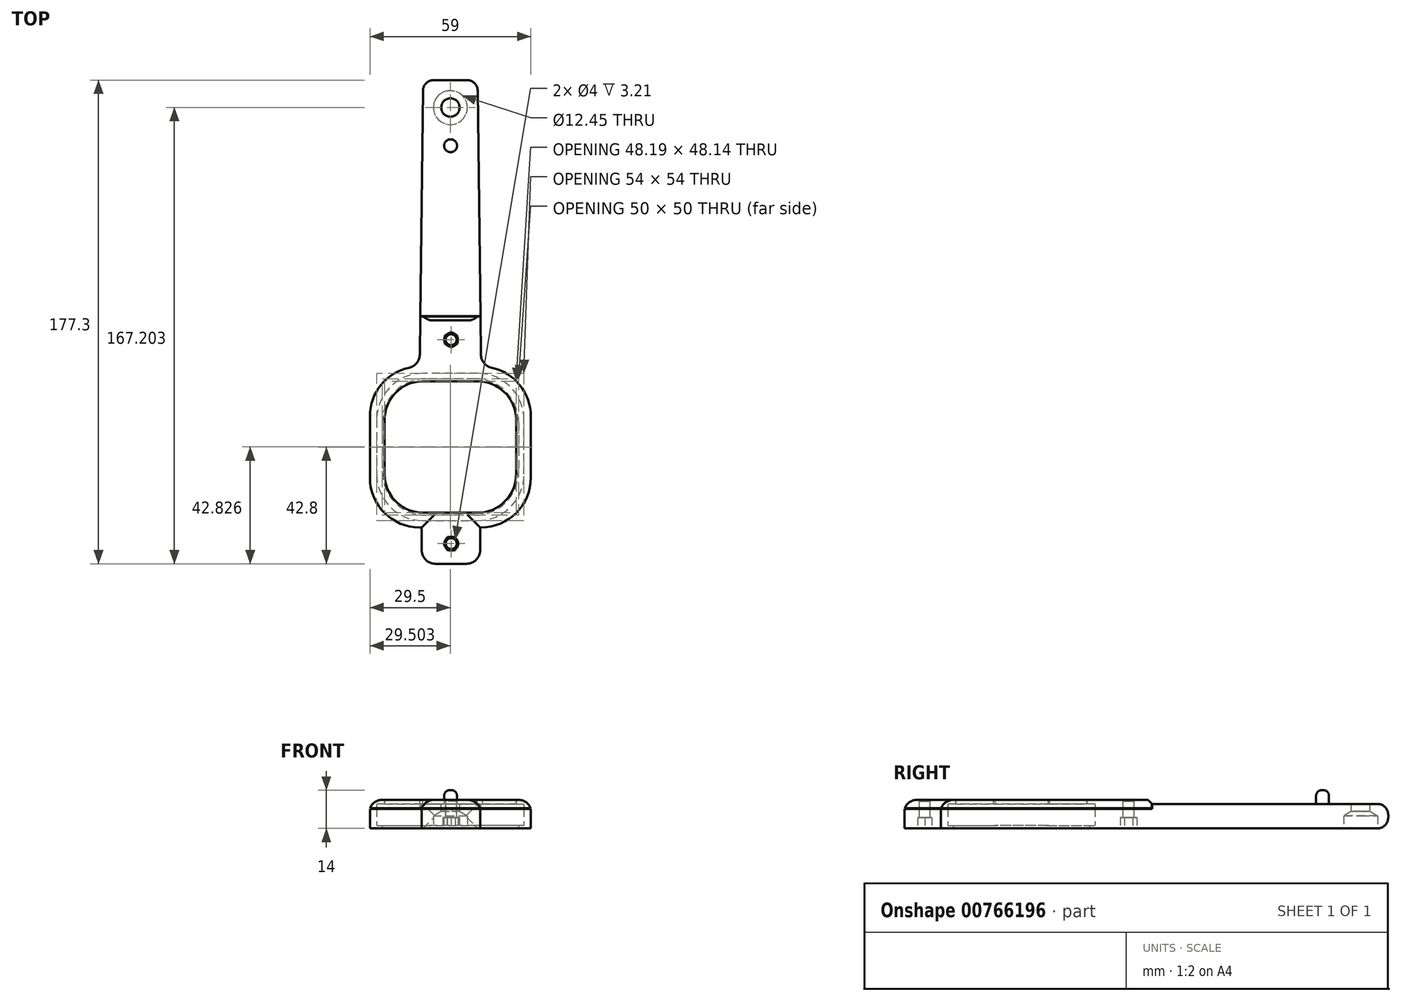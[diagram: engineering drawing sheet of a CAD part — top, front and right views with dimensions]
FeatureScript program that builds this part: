
annotation { "Feature Type Name" : "Feature", "Feature Type Description" : "" }
export const myFeature = defineFeature(function(context is Context, id is Id, definition is map)
    precondition{}
    {
        {
            var Q0;
            Q0=qCreatedBy(makeId("Top.planeOp"),FACE);
            var sketch = newSketch(context, id + "F0", { "sketchPlane" : qUnion([Q0])});
            skLineSegment(sketch, "E0.bottom", {"start": v(17, 0) * mm, "end": v(37, 0) * mm});
            skLineSegment(sketch, "E0.top", {"start": v(17, -54) * mm, "end": v(37, -54) * mm});
            skLineSegment(sketch, "E0.left", {"start": v(0, -17) * mm, "end": v(0, -37) * mm});
            skLineSegment(sketch, "E0.right", {"start": v(54, -17) * mm, "end": v(54, -37) * mm});
            skPoint(sketch, "E1.visualSharp", {"position": v(0, 0) * mm});
            skArc(sketch, "E1.filletArc", {"start": v(17, 0) * mm, "mid": v(4.98, -4.98) * mm, "end": v(0, -17) * mm});
            skPoint(sketch, "E2.visualSharp", {"position": v(54, 0) * mm});
            skArc(sketch, "E2.filletArc", {"start": v(54, -17) * mm, "mid": v(49.02, -4.98) * mm, "end": v(37, 0) * mm});
            skPoint(sketch, "E3.visualSharp", {"position": v(54, -54) * mm});
            skArc(sketch, "E3.filletArc", {"start": v(37, -54) * mm, "mid": v(49.02, -49.02) * mm, "end": v(54, -37) * mm});
            skPoint(sketch, "E4.visualSharp", {"position": v(0, -54) * mm});
            skArc(sketch, "E4.filletArc", {"start": v(0, -37) * mm, "mid": v(4.98, -49.02) * mm, "end": v(17, -54) * mm});
            skLineSegment(sketch, "E5.bottom", {"start": v(15.75, 2.5) * mm, "end": v(38.25, 2.5) * mm});
            skLineSegment(sketch, "E5.top", {"start": v(15.75, -56.5) * mm, "end": v(38.25, -56.5) * mm});
            skLineSegment(sketch, "E5.left", {"start": v(-2.5, -15.75) * mm, "end": v(-2.5, -38.25) * mm});
            skLineSegment(sketch, "E5.right", {"start": v(56.5, -15.75) * mm, "end": v(56.5, -38.25) * mm});
            skPoint(sketch, "E6.visualSharp", {"position": v(-2.5, 2.5) * mm});
            skArc(sketch, "E6.filletArc", {"start": v(15.75, 2.5) * mm, "mid": v(2.85, -2.85) * mm, "end": v(-2.5, -15.75) * mm});
            skPoint(sketch, "E7.visualSharp", {"position": v(56.5, 2.5) * mm});
            skArc(sketch, "E7.filletArc", {"start": v(56.5, -15.75) * mm, "mid": v(51.15, -2.85) * mm, "end": v(38.25, 2.5) * mm});
            skPoint(sketch, "E8.visualSharp", {"position": v(56.5, -56.5) * mm});
            skArc(sketch, "E8.filletArc", {"start": v(38.25, -56.5) * mm, "mid": v(51.15, -51.15) * mm, "end": v(56.5, -38.25) * mm});
            skPoint(sketch, "E9.visualSharp", {"position": v(-2.5, -56.5) * mm});
            skArc(sketch, "E9.filletArc", {"start": v(-2.5, -38.25) * mm, "mid": v(2.85, -51.15) * mm, "end": v(15.75, -56.5) * mm});
            skLineSegment(sketch, "E10", {"start": v(38.25, 2.5) * mm, "end": v(37, 107.5) * mm});
            skLineSegment(sketch, "E11", {"start": v(37, 107.5) * mm, "end": v(17, 107.5) * mm});
            skLineSegment(sketch, "E12", {"start": v(17, 107.5) * mm, "end": v(15.75, 2.5) * mm});
            skPoint(sketch, "E13.startSnap0", {"position": v(27, 107.5) * mm});
            skPoint(sketch, "E13.end.orphan", {"position": v(27, 107.5) * mm});
            skPoint(sketch, "E13.start.orphan", {"position": v(27, 2.5) * mm});
            skSolve(sketch);
        }
        {
            var Q0;
            Q0=makeQuery(id+"F0.imprint","IMPRINT",FACE,{"disambiguationData":[TD([[makeQuery(id+"F0.imprint","IMPRINT",EDGE,{"derivedFrom":sQuery(id+"F0.wireOp",EDGE,"E0.bottom")}),1.0]])]});
            extrude(context, id + "F1", {"entities" : qUnion([Q0]), "depth" : 9 * mm, "offsetDistance" : 25 * mm});
        }
        {
            var Q0;
            Q0=makeQuery(id+"F1.opExtrude","CAP_FACE",FACE,{"disambiguationData":[OSD([sQuery(id+"F0.wireOp",EDGE,"E0.bottom"),sQuery(id+"F0.wireOp",EDGE,"E0.top"),sQuery(id+"F0.wireOp",EDGE,"E0.left"),sQuery(id+"F0.wireOp",EDGE,"E0.right"),sQuery(id+"F0.wireOp",EDGE,"E1.filletArc"),sQuery(id+"F0.wireOp",EDGE,"E2.filletArc"),sQuery(id+"F0.wireOp",EDGE,"E3.filletArc"),sQuery(id+"F0.wireOp",EDGE,"E4.filletArc"),sQuery(id+"F0.wireOp",EDGE,"E5.bottom"),sQuery(id+"F0.wireOp",EDGE,"E5.top"),sQuery(id+"F0.wireOp",EDGE,"E5.left"),sQuery(id+"F0.wireOp",EDGE,"E5.right"),sQuery(id+"F0.wireOp",EDGE,"E6.filletArc"),sQuery(id+"F0.wireOp",EDGE,"E7.filletArc"),sQuery(id+"F0.wireOp",EDGE,"E8.filletArc"),sQuery(id+"F0.wireOp",EDGE,"E9.filletArc")])],"isStart":true});
            var sketch = newSketch(context, id + "F2", { "sketchPlane" : qUnion([Q0])});
            skLineSegment(sketch, "E14.bottom", {"start": v(37.7, 0) * mm, "end": v(16.48, 0) * mm});
            skLineSegment(sketch, "E14.top", {"start": v(37.7, 56) * mm, "end": v(16.48, 56) * mm});
            skLineSegment(sketch, "E14.left", {"start": v(55.96, 18.25) * mm, "end": v(55.96, 37.75) * mm});
            skLineSegment(sketch, "E14.right", {"start": v(-1.77, 18.25) * mm, "end": v(-1.77, 37.75) * mm});
            skPoint(sketch, "E15.visualSharp", {"position": v(-1.77, 0) * mm});
            skArc(sketch, "E15.filletArc", {"start": v(-1.77, 18.25) * mm, "mid": v(3.58, 5.35) * mm, "end": v(16.48, 0) * mm});
            skPoint(sketch, "E16.visualSharp", {"position": v(-1.77, 56) * mm});
            skArc(sketch, "E16.filletArc", {"start": v(16.48, 56) * mm, "mid": v(3.58, 50.65) * mm, "end": v(-1.77, 37.75) * mm});
            skPoint(sketch, "E17.visualSharp", {"position": v(55.96, 56) * mm});
            skArc(sketch, "E17.filletArc", {"start": v(55.96, 37.75) * mm, "mid": v(50.61, 50.65) * mm, "end": v(37.7, 56) * mm});
            skPoint(sketch, "E18.visualSharp", {"position": v(55.96, 0) * mm});
            skArc(sketch, "E18.filletArc", {"start": v(37.7, 0) * mm, "mid": v(50.61, 5.35) * mm, "end": v(55.96, 18.25) * mm});
            skLineSegment(sketch, "E19.bottom", {"start": v(36, 2) * mm, "end": v(18, 2) * mm});
            skLineSegment(sketch, "E19.top", {"start": v(36, 52) * mm, "end": v(18, 52) * mm});
            skLineSegment(sketch, "E19.left", {"start": v(52, 18) * mm, "end": v(52, 36) * mm});
            skLineSegment(sketch, "E19.right", {"start": v(2, 18) * mm, "end": v(2, 36) * mm});
            skPoint(sketch, "E20.visualSharp", {"position": v(52, 2) * mm});
            skArc(sketch, "E20.filletArc", {"start": v(36, 2) * mm, "mid": v(47.31, 6.69) * mm, "end": v(52, 18) * mm});
            skPoint(sketch, "E21.visualSharp", {"position": v(2, 2) * mm});
            skArc(sketch, "E21.filletArc", {"start": v(2, 18) * mm, "mid": v(6.69, 6.69) * mm, "end": v(18, 2) * mm});
            skPoint(sketch, "E22.visualSharp", {"position": v(2, 52) * mm});
            skArc(sketch, "E22.filletArc", {"start": v(18, 52) * mm, "mid": v(6.69, 47.31) * mm, "end": v(2, 36) * mm});
            skPoint(sketch, "E23.visualSharp", {"position": v(52, 52) * mm});
            skArc(sketch, "E23.filletArc", {"start": v(52, 36) * mm, "mid": v(47.31, 47.31) * mm, "end": v(36, 52) * mm});
            skSolve(sketch);
        }
        {
            var Q0;
            Q0=makeQuery(id+"F2.imprint","IMPRINT",FACE,{"disambiguationData":[TD([[makeQuery(id+"F2.imprint","IMPRINT",EDGE,{"derivedFrom":sQuery(id+"F2.wireOp",EDGE,"E19.bottom")}),1.0]])]});
            extrude(context, id + "F3", {"entities" : qUnion([Q0]), "operationType" : NewBodyOperationType.ADD, "oppositeDirection" : true, "depth" : 1 * mm, "offsetDistance" : 25 * mm});
        }
        {
            var Q0;
            Q0=makeQuery(id+"F1.opExtrude","CAP_FACE",FACE,{"disambiguationData":[OSD([sQuery(id+"F0.wireOp",EDGE,"E0.bottom"),sQuery(id+"F0.wireOp",EDGE,"E0.top"),sQuery(id+"F0.wireOp",EDGE,"E0.left"),sQuery(id+"F0.wireOp",EDGE,"E0.right"),sQuery(id+"F0.wireOp",EDGE,"E1.filletArc"),sQuery(id+"F0.wireOp",EDGE,"E2.filletArc"),sQuery(id+"F0.wireOp",EDGE,"E3.filletArc"),sQuery(id+"F0.wireOp",EDGE,"E4.filletArc"),sQuery(id+"F0.wireOp",EDGE,"E5.bottom"),sQuery(id+"F0.wireOp",EDGE,"E5.top"),sQuery(id+"F0.wireOp",EDGE,"E5.left"),sQuery(id+"F0.wireOp",EDGE,"E5.right"),sQuery(id+"F0.wireOp",EDGE,"E6.filletArc"),sQuery(id+"F0.wireOp",EDGE,"E7.filletArc"),sQuery(id+"F0.wireOp",EDGE,"E8.filletArc"),sQuery(id+"F0.wireOp",EDGE,"E9.filletArc")])],"isStart":false});
            var sketch = newSketch(context, id + "F4", { "sketchPlane" : qUnion([Q0])});
            skLineSegment(sketch, "E24.bottom", {"start": v(15.75, -56.5) * mm, "end": v(38.68, -56.5) * mm});
            skLineSegment(sketch, "E24.top", {"start": v(15.75, -51) * mm, "end": v(38.68, -51) * mm});
            skLineSegment(sketch, "E24.left", {"start": v(15.75, -56.5) * mm, "end": v(15.75, -51) * mm});
            skLineSegment(sketch, "E24.right", {"start": v(38.68, -56.5) * mm, "end": v(38.68, -51) * mm});
            skPoint(sketch, "E25", {"position": v(27.03, 97.4) * mm});
            skLineSegment(sketch, "E26.0", {"start": v(37, 107.5) * mm, "end": v(17, 107.5) * mm});
            skSolve(sketch);
        }
        {
            var Q0;
            {var subQ5=makeQuery(id+"F1.opExtrude","CAP_EDGE",EDGE,{"disambiguationData":[OSD([sQuery(id+"F0.wireOp",EDGE,"E0.top")])],"isStart":false});Q0=makeQuery(id+"F4.imprint","IMPRINT",FACE,{"disambiguationData":[TD([[makeQuery(id+"F4.imprint","IMPRINT",EDGE,{"derivedFrom":subQ5}),-1.0]])]});}
            var Q1;
            {var subQ2=sQuery(id+"F4.wireOp",EDGE,"E24.top");Q1=makeQuery(id+"F4.imprint","IMPRINT",FACE,{"disambiguationData":[TD([[makeQuery(id+"F4.imprint","IMPRINT",EDGE,{"derivedFrom":subQ2}),-1.0]])]});}
            extrude(context, id + "F5", {"entities" : qUnion([Q0, Q1]), "operationType" : NewBodyOperationType.ADD, "depth" : 1.5 * mm, "offsetDistance" : 25 * mm});
        }
        {
            var Q0;
            Q0=makeQuery(id+"F0.imprint","IMPRINT",FACE,{"disambiguationData":[TD([[makeQuery(id+"F0.imprint","IMPRINT",EDGE,{"derivedFrom":sQuery(id+"F0.wireOp",EDGE,"E5.bottom")}),1.0]])]});
            extrude(context, id + "F6", {"entities" : qUnion([Q0]), "operationType" : NewBodyOperationType.ADD, "depth" : 9 * mm, "offsetDistance" : 25 * mm});
        }
        {
            var Q0;
            {var subQ0=sQuery(id+"F0.wireOp",EDGE,"E10");var subQ1=sQuery(id+"F0.wireOp",EDGE,"E7.filletArc");var subQ2=sQuery(id+"F0.wireOp",EDGE,"E5.bottom");Q0=makeQuery(id+"F6.boolean.opBoolean","MERGE",EDGE,{"derivedFrom":[makeQuery(id+"Fi0xQTKt3oh8g8N_1.boolean.opBoolean","MERGE",EDGE,{"derivedFrom":[makeQuery(id+"F1.opExtrude","SWEPT_EDGE",EDGE,{"disambiguationData":[OSD([subQ2,subQ1,subQ0])]}),makeQuery(id+"Fi0xQTKt3oh8g8N_1.opExtrude","SWEPT_EDGE",EDGE,{"disambiguationData":[OSD([subQ1,sQuery(id+"Fwkhj9xOdCnqwH3_1.wireOp",EDGE,"TBOp4eyl-GCsp-HRSN-tsRw-HrjPXPLde6vr.bottom")])]})]}),makeQuery(id+"F6.opExtrude","SWEPT_EDGE",EDGE,{"disambiguationData":[OSD([subQ2,subQ1,subQ0])]})]});}
            var Q1;
            {var subQ0=sQuery(id+"F0.wireOp",EDGE,"E12");var subQ1=sQuery(id+"F0.wireOp",EDGE,"E6.filletArc");var subQ2=sQuery(id+"F0.wireOp",EDGE,"E5.bottom");Q1=makeQuery(id+"F6.boolean.opBoolean","MERGE",EDGE,{"derivedFrom":[makeQuery(id+"F1.opExtrude","SWEPT_EDGE",EDGE,{"disambiguationData":[OSD([subQ2,subQ1,subQ0])]}),makeQuery(id+"F6.opExtrude","SWEPT_EDGE",EDGE,{"disambiguationData":[OSD([subQ2,subQ1,subQ0])]})]});}
            fillet(context, id + "F7", {"entities" : qUnion([Q0, Q1]), "radius" : 5 * mm, "tangentPropagation" : true, "allowEdgeOverflow" : false});
        }
        {
            var Q0;
            Q0=sQuery(id+"F4.wireOp",VERTEX,"E25");
            var Q1;
            Q1=makeQuery(id+"F1.opExtrude","SWEPT_BODY",BODY,{"disambiguationData":[OSD([sQuery(id+"F0.wireOp",EDGE,"E0.bottom"),sQuery(id+"F0.wireOp",EDGE,"E0.top"),sQuery(id+"F0.wireOp",EDGE,"E0.left"),sQuery(id+"F0.wireOp",EDGE,"E0.right"),sQuery(id+"F0.wireOp",EDGE,"E1.filletArc"),sQuery(id+"F0.wireOp",EDGE,"E2.filletArc"),sQuery(id+"F0.wireOp",EDGE,"E3.filletArc"),sQuery(id+"F0.wireOp",EDGE,"E4.filletArc"),sQuery(id+"F0.wireOp",EDGE,"E5.bottom"),sQuery(id+"F0.wireOp",EDGE,"E5.top"),sQuery(id+"F0.wireOp",EDGE,"E5.left"),sQuery(id+"F0.wireOp",EDGE,"E5.right"),sQuery(id+"F0.wireOp",EDGE,"E6.filletArc"),sQuery(id+"F0.wireOp",EDGE,"E7.filletArc"),sQuery(id+"F0.wireOp",EDGE,"E8.filletArc"),sQuery(id+"F0.wireOp",EDGE,"E9.filletArc")])]});
            hole(context, id + "F8", {"style" : HoleStyle.SIMPLE, "endStyle" : HoleEndStyle.BLIND, "standardTappedOrClearance" : lookupTablePath({ "fit" : "Free", "standard" : "ANSI", "size" : "1/4", "type" : "Clearance" }), "standardBlindInLast" : lookupTablePath({ "fit" : "Free", "standard" : "ANSI", "size" : "1/4", "type" : "Clearance" }), "holeDiameter" : 6.76 * mm, "majorDiameter" : 5 * mm, "holeDepth" : 50 * mm, "isTappedThrough" : true, "tappedDepth" : 12 * mm, "tapClearance" : 3, "locations" : qUnion([Q0]), "scope" : qUnion([Q1])});
        }
        {
            var Q0;
            Q0=makeQuery(id+"F0.imprint","IMPRINT",FACE,{"disambiguationData":[TD([[makeQuery(id+"F0.imprint","IMPRINT",EDGE,{"derivedFrom":sQuery(id+"F0.wireOp",EDGE,"E5.bottom")}),1.0]])]});
            var sketch = newSketch(context, id + "F9", { "sketchPlane" : qUnion([Q0])});
            skPoint(sketch, "E27", {"position": v(27, 97.4) * mm});
            skLineSegment(sketch, "E28", {"start": v(16.85, 83.42) * mm, "end": v(37.33, 83.42) * mm});
            skPoint(sketch, "E29", {"position": v(27.09, 83.42) * mm});
            skCircle(sketch, "E30", {"center": v(27.09, 83.42) * mm, "radius": 2.38 * mm});
            skPoint(sketch, "E31.0", {"position": v(27.03, 97.4) * mm});
            skSolve(sketch);
        }
        {
            var Q0;
            Q0=sQuery(id+"F9.wireOp",VERTEX,"E27");
            var Q1;
            Q1=makeQuery(id+"F1.opExtrude","SWEPT_BODY",BODY,{"disambiguationData":[OSD([sQuery(id+"F0.wireOp",EDGE,"E0.bottom"),sQuery(id+"F0.wireOp",EDGE,"E0.top"),sQuery(id+"F0.wireOp",EDGE,"E0.left"),sQuery(id+"F0.wireOp",EDGE,"E0.right"),sQuery(id+"F0.wireOp",EDGE,"E1.filletArc"),sQuery(id+"F0.wireOp",EDGE,"E2.filletArc"),sQuery(id+"F0.wireOp",EDGE,"E3.filletArc"),sQuery(id+"F0.wireOp",EDGE,"E4.filletArc"),sQuery(id+"F0.wireOp",EDGE,"E5.bottom"),sQuery(id+"F0.wireOp",EDGE,"E5.top"),sQuery(id+"F0.wireOp",EDGE,"E5.left"),sQuery(id+"F0.wireOp",EDGE,"E5.right"),sQuery(id+"F0.wireOp",EDGE,"E6.filletArc"),sQuery(id+"F0.wireOp",EDGE,"E7.filletArc"),sQuery(id+"F0.wireOp",EDGE,"E8.filletArc"),sQuery(id+"F0.wireOp",EDGE,"E9.filletArc")])]});
            hole(context, id + "F10", {"style" : HoleStyle.SIMPLE, "endStyle" : HoleEndStyle.BLIND, "oppositeDirection" : true, "holeDiameter" : 12.45 * mm, "majorDiameter" : 5 * mm, "holeDepth" : 4.57 * mm, "isTappedThrough" : true, "tappedDepth" : 12 * mm, "tapClearance" : 3, "locations" : qUnion([Q0]), "scope" : qUnion([Q1])});
        }
        {
            var Q0;
            {var subQ0=sQuery(id+"F0.wireOp",EDGE,"E5.bottom");var subQ1=sQuery(id+"F0.wireOp",EDGE,"E6.filletArc");var subQ2=sQuery(id+"F0.wireOp",EDGE,"E5.left");var subQ3=sQuery(id+"F0.wireOp",EDGE,"E5.top");var subQ4=sQuery(id+"F0.wireOp",EDGE,"E0.bottom");var subQ5=sQuery(id+"F0.wireOp",EDGE,"E0.left");var subQ6=sQuery(id+"F0.wireOp",EDGE,"E4.filletArc");var subQ8=sQuery(id+"F0.wireOp",EDGE,"E9.filletArc");var subQ11=sQuery(id+"F0.wireOp",EDGE,"E8.filletArc");var subQ12=sQuery(id+"F0.wireOp",EDGE,"E1.filletArc");var subQ14=sQuery(id+"F0.wireOp",EDGE,"E7.filletArc");Q0=makeQuery(id+"F6.boolean.opBoolean","MERGE",FACE,{"derivedFrom":[makeQuery(id+"F5.boolean.opBoolean","SPLIT",FACE,{"disambiguationData":[TD([makeQuery(id+"F1.opExtrude","SWEPT_FACE",FACE,{"disambiguationData":[OSD([subQ4])]})])],"derivedFrom":makeQuery(id+"F1.opExtrude","CAP_FACE",FACE,{"disambiguationData":[OSD([subQ4,sQuery(id+"F0.wireOp",EDGE,"E0.top"),subQ5,sQuery(id+"F0.wireOp",EDGE,"E0.right"),subQ12,sQuery(id+"F0.wireOp",EDGE,"E2.filletArc"),sQuery(id+"F0.wireOp",EDGE,"E3.filletArc"),subQ6,subQ0,subQ3,subQ2,sQuery(id+"F0.wireOp",EDGE,"E5.right"),subQ1,subQ14,subQ11,subQ8])],"isStart":false})}),makeQuery(id+"F6.opExtrude","CAP_FACE",FACE,{"disambiguationData":[OSD([subQ0,sQuery(id+"F0.wireOp",EDGE,"E10"),sQuery(id+"F0.wireOp",EDGE,"E11"),sQuery(id+"F0.wireOp",EDGE,"E12")])],"isStart":false})]});}
            var sketch = newSketch(context, id + "F11", { "sketchPlane" : qUnion([Q0])});
            skCircle(sketch, "E32", {"center": v(27.09, 83.42) * mm, "radius": 2.36 * mm});
            skCircle(sketch, "E33.0", {"center": v(27.09, 83.42) * mm, "radius": 2.38 * mm});
            skSolve(sketch);
        }
        {
            var Q0;
            {var subQ0=sQuery(id+"F11.wireOp",EDGE,"E33.0");var subQ1=sQuery(id+"F11.wireOp",EDGE,"E32");var subQ2=makeQuery(id+"F11.imprint","INTERSECT",VERTEX,{"disambiguationData":[OD(0.0)],"derivedFrom":[subQ1,subQ0]});Q0=makeQuery(id+"F11.imprint","IMPRINT",FACE,{"disambiguationData":[TD([[makeQuery(id+"F11.imprint","IMPRINT",EDGE,{"disambiguationData":[TD([[subQ2,1.0]])],"derivedFrom":subQ1}),1.0]])]});}
            extrude(context, id + "F12", {"entities" : qUnion([Q0]), "operationType" : NewBodyOperationType.ADD, "depth" : 5 * mm, "offsetDistance" : 25 * mm});
        }
        {
            var Q0;
            Q0=makeQuery(id+"F12.opExtrude","CAP_EDGE",EDGE,{"disambiguationData":[OSD([sQuery(id+"F11.wireOp",EDGE,"E32")])],"isStart":false});
            fillet(context, id + "F13", {"entities" : qUnion([Q0]), "radius" : 2 * mm, "tangentPropagation" : true, "allowEdgeOverflow" : false});
        }
        {
            var Q0;
            Q0=makeQuery(id+"F6.opExtrude","CAP_EDGE",EDGE,{"disambiguationData":[OSD([sQuery(id+"F0.wireOp",EDGE,"E11")])],"isStart":false});
            var Q1;
            Q1=makeQuery(id+"F6.opExtrude","SWEPT_EDGE",EDGE,{"disambiguationData":[OSD([sQuery(id+"F0.wireOp",EDGE,"E11"),sQuery(id+"F0.wireOp",EDGE,"E12")])]});
            var Q2;
            Q2=makeQuery(id+"F6.opExtrude","SWEPT_EDGE",EDGE,{"disambiguationData":[OSD([sQuery(id+"F0.wireOp",EDGE,"E10"),sQuery(id+"F0.wireOp",EDGE,"E11")])]});
            var Q3;
            Q3=makeQuery(id+"F6.opExtrude","CAP_EDGE",EDGE,{"disambiguationData":[OSD([sQuery(id+"F0.wireOp",EDGE,"E11")])],"isStart":true});
            fillet(context, id + "F14", {"entities" : qUnion([Q0, Q1, Q2, Q3]), "radius" : 4 * mm, "allowEdgeOverflow" : false});
        }
        {
            var Q0;
            Q0=makeQuery(id+"F5.opExtrude","CAP_FACE",FACE,{"disambiguationData":[OSD([sQuery(id+"F0.wireOp",EDGE,"E8.filletArc"),sQuery(id+"F4.wireOp",EDGE,"E24.bottom"),sQuery(id+"F4.wireOp",EDGE,"E24.top"),sQuery(id+"F4.wireOp",EDGE,"E24.left"),sQuery(id+"F4.wireOp",EDGE,"E24.right")])],"isStart":false});
            var sketch = newSketch(context, id + "F15", { "sketchPlane" : qUnion([Q0])});
            skLineSegment(sketch, "E34", {"start": v(16.5, -56.5) * mm, "end": v(16.5, -69.8) * mm});
            skLineSegment(sketch, "E35", {"start": v(16.5, -69.8) * mm, "end": v(37.93, -69.8) * mm});
            skLineSegment(sketch, "E36", {"start": v(37.93, -69.8) * mm, "end": v(37.93, -56.5) * mm});
            skPoint(sketch, "E37", {"position": v(27.33, -62.41) * mm});
            skPoint(sketch, "E38", {"position": v(27.26, 12.32) * mm});
            skSolve(sketch);
        }
        {
            var Q0;
            Q0=makeQuery(id+"F15.imprint","IMPRINT",FACE,{"disambiguationData":[TD([[makeQuery(id+"F15.imprint","IMPRINT",EDGE,{"derivedFrom":sQuery(id+"F15.wireOp",EDGE,"E34")}),1.0]])]});
            extrude(context, id + "F16", {"entities" : qUnion([Q0]), "operationType" : NewBodyOperationType.ADD, "oppositeDirection" : true, "depth" : 10.5 * mm, "offsetDistance" : 25 * mm});
        }
        {
            var Q0;
            Q0=makeQuery(id+"F16.opExtrude","SWEPT_EDGE",EDGE,{"disambiguationData":[OSD([sQuery(id+"F15.wireOp",EDGE,"E34"),sQuery(id+"F15.wireOp",EDGE,"E35")])]});
            var Q1;
            Q1=makeQuery(id+"F16.opExtrude","SWEPT_EDGE",EDGE,{"disambiguationData":[OSD([sQuery(id+"F15.wireOp",EDGE,"E35"),sQuery(id+"F15.wireOp",EDGE,"E36")])]});
            fillet(context, id + "F17", {"entities" : qUnion([Q0, Q1]), "radius" : 5 * mm, "tangentPropagation" : true, "allowEdgeOverflow" : false});
        }
        {
            var Q0;
            Q0=sQuery(id+"F15.wireOp",VERTEX,"E37");
            var Q1;
            Q1=makeQuery(id+"F1.opExtrude","SWEPT_BODY",BODY,{"disambiguationData":[OSD([sQuery(id+"F0.wireOp",EDGE,"E0.bottom"),sQuery(id+"F0.wireOp",EDGE,"E0.top"),sQuery(id+"F0.wireOp",EDGE,"E0.left"),sQuery(id+"F0.wireOp",EDGE,"E0.right"),sQuery(id+"F0.wireOp",EDGE,"E1.filletArc"),sQuery(id+"F0.wireOp",EDGE,"E2.filletArc"),sQuery(id+"F0.wireOp",EDGE,"E3.filletArc"),sQuery(id+"F0.wireOp",EDGE,"E4.filletArc"),sQuery(id+"F0.wireOp",EDGE,"E5.bottom"),sQuery(id+"F0.wireOp",EDGE,"E5.top"),sQuery(id+"F0.wireOp",EDGE,"E5.left"),sQuery(id+"F0.wireOp",EDGE,"E5.right"),sQuery(id+"F0.wireOp",EDGE,"E6.filletArc"),sQuery(id+"F0.wireOp",EDGE,"E7.filletArc"),sQuery(id+"F0.wireOp",EDGE,"E8.filletArc"),sQuery(id+"F0.wireOp",EDGE,"E9.filletArc")])]});
            hole(context, id + "F18", {"style" : HoleStyle.C_SINK, "endStyle" : HoleEndStyle.BLIND, "holeDiameter" : 4 * mm, "cSinkDiameter" : 5 * mm, "cSinkAngle" : 90 * degree, "majorDiameter" : 5 * mm, "holeDepth" : 20 * mm, "isTappedThrough" : true, "tappedDepth" : 12 * mm, "tapClearance" : 3, "locations" : qUnion([Q0]), "scope" : qUnion([Q1])});
        }
        {
            var Q0;
            {var subQ0=sQuery(id+"F0.wireOp",EDGE,"E5.bottom");var subQ1=sQuery(id+"F0.wireOp",EDGE,"E4.filletArc");var subQ2=sQuery(id+"F0.wireOp",EDGE,"E3.filletArc");var subQ3=sQuery(id+"F0.wireOp",EDGE,"E2.filletArc");var subQ4=sQuery(id+"F0.wireOp",EDGE,"E1.filletArc");var subQ5=sQuery(id+"F0.wireOp",EDGE,"E0.right");var subQ6=sQuery(id+"F0.wireOp",EDGE,"E0.left");var subQ7=sQuery(id+"F0.wireOp",EDGE,"E0.top");Q0=makeQuery(id+"F16.boolean.opBoolean","MERGE",FACE,{"derivedFrom":[makeQuery(id+"F6.boolean.opBoolean","MERGE",FACE,{"derivedFrom":[makeQuery(id+"F3.boolean.opBoolean","MERGE",FACE,{"derivedFrom":[makeQuery(id+"F1.opExtrude","CAP_FACE",FACE,{"disambiguationData":[OSD([sQuery(id+"F0.wireOp",EDGE,"E0.bottom"),subQ7,subQ6,subQ5,subQ4,subQ3,subQ2,subQ1,subQ0,sQuery(id+"F0.wireOp",EDGE,"E5.top"),sQuery(id+"F0.wireOp",EDGE,"E5.left"),sQuery(id+"F0.wireOp",EDGE,"E5.right"),sQuery(id+"F0.wireOp",EDGE,"E6.filletArc"),sQuery(id+"F0.wireOp",EDGE,"E7.filletArc"),sQuery(id+"F0.wireOp",EDGE,"E8.filletArc"),sQuery(id+"F0.wireOp",EDGE,"E9.filletArc")])],"isStart":true}),makeQuery(id+"F3.opExtrude","CAP_FACE",FACE,{"disambiguationData":[OSD([subQ7,subQ6,subQ5,subQ4,subQ3,subQ2,subQ1,sQuery(id+"F2.wireOp",EDGE,"E14.bottom"),sQuery(id+"F2.wireOp",EDGE,"E19.bottom"),sQuery(id+"F2.wireOp",EDGE,"E19.top"),sQuery(id+"F2.wireOp",EDGE,"E19.left"),sQuery(id+"F2.wireOp",EDGE,"E19.right"),sQuery(id+"F2.wireOp",EDGE,"E20.filletArc"),sQuery(id+"F2.wireOp",EDGE,"E21.filletArc"),sQuery(id+"F2.wireOp",EDGE,"E22.filletArc"),sQuery(id+"F2.wireOp",EDGE,"E23.filletArc")])],"isStart":true})]}),makeQuery(id+"F6.opExtrude","CAP_FACE",FACE,{"disambiguationData":[OSD([subQ0,sQuery(id+"F0.wireOp",EDGE,"E10"),sQuery(id+"F0.wireOp",EDGE,"E11"),sQuery(id+"F0.wireOp",EDGE,"E12")])],"isStart":true})]}),makeQuery(id+"F16.opExtrude","CAP_FACE",FACE,{"disambiguationData":[OSD([sQuery(id+"F4.wireOp",EDGE,"E24.bottom"),sQuery(id+"F15.wireOp",EDGE,"E34"),sQuery(id+"F15.wireOp",EDGE,"E35"),sQuery(id+"F15.wireOp",EDGE,"E36")])],"isStart":false})]});}
            var sketch = newSketch(context, id + "F19", { "sketchPlane" : qUnion([Q0])});
            skPoint(sketch, "E39.0", {"position": v(27.33, 62.41) * mm});
            skCircle(sketch, "E40.cCircle", {"center": v(27.33, 62.41) * mm, "radius": 2.62 * mm, "construction": true});
            skLineSegment(sketch, "E40.0", {"start": v(30.36, 62.4) * mm, "end": v(28.84, 59.78) * mm});
            skLineSegment(sketch, "E40.1", {"start": v(28.84, 59.78) * mm, "end": v(25.8, 59.8) * mm});
            skLineSegment(sketch, "E40.2", {"start": v(25.8, 59.8) * mm, "end": v(24.3, 62.42) * mm});
            skLineSegment(sketch, "E40.3", {"start": v(24.3, 62.42) * mm, "end": v(25.82, 65.04) * mm});
            skLineSegment(sketch, "E40.4", {"start": v(25.82, 65.04) * mm, "end": v(28.86, 65.03) * mm});
            skLineSegment(sketch, "E40.5", {"start": v(28.86, 65.03) * mm, "end": v(30.36, 62.4) * mm});
            skPoint(sketch, "E40.0.midPoint", {"position": v(29.6, 61.1) * mm});
            skPoint(sketch, "E41.0", {"position": v(27.26, -12.32) * mm});
            skCircle(sketch, "E42.cCircle", {"center": v(27.26, -12.32) * mm, "radius": 2.63 * mm, "construction": true});
            skLineSegment(sketch, "E42.0", {"start": v(24.62, -13.81) * mm, "end": v(24.65, -10.78) * mm});
            skLineSegment(sketch, "E42.1", {"start": v(24.65, -10.78) * mm, "end": v(27.3, -9.29) * mm});
            skLineSegment(sketch, "E42.2", {"start": v(27.3, -9.29) * mm, "end": v(29.9, -10.83) * mm});
            skLineSegment(sketch, "E42.3", {"start": v(29.9, -10.83) * mm, "end": v(29.87, -13.86) * mm});
            skLineSegment(sketch, "E42.4", {"start": v(29.87, -13.86) * mm, "end": v(27.23, -15.35) * mm});
            skLineSegment(sketch, "E42.5", {"start": v(27.23, -15.35) * mm, "end": v(24.62, -13.81) * mm});
            skPoint(sketch, "E42.0.midPoint", {"position": v(24.64, -12.3) * mm});
            skSolve(sketch);
        }
        {
            var Q0;
            Q0=makeQuery(id+"F19.imprint","IMPRINT",FACE,{"disambiguationData":[TD([[makeQuery(id+"F19.imprint","IMPRINT",EDGE,{"derivedFrom":sQuery(id+"F19.wireOp",EDGE,"E40.0")}),-1.0]])]});
            var Q1;
            Q1=makeQuery(id+"F19.imprint","IMPRINT",FACE,{"disambiguationData":[TD([[makeQuery(id+"F19.imprint","IMPRINT",EDGE,{"derivedFrom":sQuery(id+"F19.wireOp",EDGE,"E42.0")}),-1.0]])]});
            extrude(context, id + "F20", {"entities" : qUnion([Q0, Q1]), "operationType" : NewBodyOperationType.REMOVE, "oppositeDirection" : true, "depth" : 4 * mm, "offsetDistance" : 25 * mm});
        }
        {
            var Q0;
            Q0=qCreatedBy(makeId("Right.planeOp"),FACE);
            var sketch = newSketch(context, id + "F21", { "sketchPlane" : qUnion([Q0])});
            skLineSegment(sketch, "E43.bottom", {"start": v(-70.6, 7.36) * mm, "end": v(20.88, 7.36) * mm});
            skLineSegment(sketch, "E43.top", {"start": v(-70.6, 7.21) * mm, "end": v(20.98, 7.21) * mm});
            skLineSegment(sketch, "E43.left", {"start": v(-70.6, 7.36) * mm, "end": v(-70.6, 7.21) * mm});
            skLineSegment(sketch, "E43.right", {"start": v(20.98, 7.36) * mm, "end": v(20.98, 7.21) * mm});
            skLineSegment(sketch, "E44", {"start": v(20.98, 7.36) * mm, "end": v(20.98, 10.1) * mm});
            skLineSegment(sketch, "E45", {"start": v(20.98, 10.1) * mm, "end": v(20.88, 10.1) * mm});
            skLineSegment(sketch, "E46", {"start": v(20.88, 10.1) * mm, "end": v(20.88, 7.36) * mm});
            skSolve(sketch);
        }
        {
            var Q0;
            Q0=makeQuery(id+"F21.imprint","IMPRINT",FACE,{"disambiguationData":[TD([[makeQuery(id+"F21.imprint","IMPRINT",EDGE,{"derivedFrom":sQuery(id+"F21.wireOp",EDGE,"E43.bottom")}),-1.0]])]});
            extrude(context, id + "F22", {"entities" : qUnion([Q0]), "operationType" : NewBodyOperationType.REMOVE, "endBound" : BoundingType.SYMMETRIC, "depth" : 150 * mm, "offsetDistance" : 25 * mm});
        }
        {
            var Q0;
            {var subQ8=sQuery(id+"F0.wireOp",EDGE,"E7.filletArc");var subQ10=sQuery(id+"F0.wireOp",EDGE,"E8.filletArc");var subQ13=sQuery(id+"F0.wireOp",EDGE,"E9.filletArc");var subQ15=sQuery(id+"F0.wireOp",EDGE,"E1.filletArc");var subQ17=sQuery(id+"F0.wireOp",EDGE,"E0.left");var subQ19=sQuery(id+"F0.wireOp",EDGE,"E12");var subQ20=sQuery(id+"F0.wireOp",EDGE,"E6.filletArc");var subQ21=sQuery(id+"F0.wireOp",EDGE,"E5.bottom");var subQ22=sQuery(id+"F0.wireOp",EDGE,"E5.left");var subQ23=sQuery(id+"F0.wireOp",EDGE,"E5.top");var subQ24=sQuery(id+"F0.wireOp",EDGE,"E4.filletArc");var subQ25=sQuery(id+"F0.wireOp",EDGE,"E0.bottom");var subQ26=makeQuery(id+"F1.opExtrude","CAP_FACE",FACE,{"disambiguationData":[OSD([subQ25,sQuery(id+"F0.wireOp",EDGE,"E0.top"),subQ17,sQuery(id+"F0.wireOp",EDGE,"E0.right"),subQ15,sQuery(id+"F0.wireOp",EDGE,"E2.filletArc"),sQuery(id+"F0.wireOp",EDGE,"E3.filletArc"),subQ24,subQ21,subQ23,subQ22,sQuery(id+"F0.wireOp",EDGE,"E5.right"),subQ20,subQ8,subQ10,subQ13])],"isStart":false});var subQ27=sQuery(id+"F0.wireOp",EDGE,"E10");var subQ28=makeQuery(id+"F1.opExtrude","SWEPT_FACE",FACE,{"disambiguationData":[OSD([subQ25])]});Q0=makeQuery(id+"F22.boolean.opBoolean","SPLIT",FACE,{"disambiguationData":[TD([subQ28])],"derivedFrom":makeQuery(id+"F6.boolean.opBoolean","MERGE",FACE,{"derivedFrom":[makeQuery(id+"F5.boolean.opBoolean","SPLIT",FACE,{"disambiguationData":[TD([subQ28])],"derivedFrom":subQ26}),makeQuery(id+"F6.opExtrude","CAP_FACE",FACE,{"disambiguationData":[OSD([subQ21,subQ27,sQuery(id+"F0.wireOp",EDGE,"E11"),subQ19])],"isStart":false})]})});}
            var Q1;
            {var subQ10=sQuery(id+"F0.wireOp",EDGE,"E0.right");var subQ11=makeQuery(id+"F1.opExtrude","CAP_EDGE",EDGE,{"disambiguationData":[OSD([subQ10])],"isStart":false});Q1=makeQuery(id+"F4.imprint","IMPRINT",FACE,{"disambiguationData":[TD([[makeQuery(id+"F4.imprint","IMPRINT",EDGE,{"derivedFrom":subQ11}),1.0]])]});}
            extrude(context, id + "F23", {"entities" : qUnion([Q0, Q1]), "operationType" : NewBodyOperationType.ADD, "depth" : 1.5 * mm, "offsetDistance" : 25 * mm});
        }
        {
            var Q0;
            Q0=makeQuery(id+"F5.opExtrude","SWEPT_FACE",FACE,{"disambiguationData":[OSD([sQuery(id+"F4.wireOp",EDGE,"E24.right")])]});
            var Q1;
            {var subQ0=sQuery(id+"F0.wireOp",EDGE,"E3.filletArc");var subQ1=makeQuery(id+"F1.opExtrude","CAP_EDGE",EDGE,{"disambiguationData":[OSD([subQ0])],"isStart":false});Q1=makeQuery(id+"F23.opExtrude","CAP_EDGE",EDGE,{"disambiguationData":[OSD([subQ0]),TDD([makeQuery(id+"F4.imprint","IMPRINT",EDGE,{"disambiguationData":[TD([[makeQuery(id+"F4.imprint","INTERSECT",VERTEX,{"derivedFrom":[makeQuery(id+"F1.opExtrude","CAP_EDGE",EDGE,{"disambiguationData":[OSD([sQuery(id+"F0.wireOp",EDGE,"E0.right")])],"isStart":false}),subQ1]}),1.0]])],"derivedFrom":subQ1})])],"isStart":false});}
            var Q2;
            {var subQ0=sQuery(id+"F0.wireOp",EDGE,"E0.right");Q2=makeQuery(id+"F23.opExtrude","CAP_EDGE",EDGE,{"disambiguationData":[OSD([subQ0]),TDD([makeQuery(id+"F4.imprint","IMPRINT",EDGE,{"derivedFrom":makeQuery(id+"F1.opExtrude","CAP_EDGE",EDGE,{"disambiguationData":[OSD([subQ0])],"isStart":false})})])],"isStart":false});}
            var Q3;
            {var subQ0=sQuery(id+"F0.wireOp",EDGE,"E2.filletArc");Q3=makeQuery(id+"F23.opExtrude","CAP_EDGE",EDGE,{"disambiguationData":[OSD([subQ0]),TDD([makeQuery(id+"F4.imprint","IMPRINT",EDGE,{"derivedFrom":makeQuery(id+"F1.opExtrude","CAP_EDGE",EDGE,{"disambiguationData":[OSD([subQ0])],"isStart":false})})])],"isStart":false});}
            var Q4;
            {var subQ0=sQuery(id+"F0.wireOp",EDGE,"E0.bottom");Q4=makeQuery(id+"F23.opExtrude","CAP_EDGE",EDGE,{"disambiguationData":[OSD([subQ0]),TDD([makeQuery(id+"F4.imprint","IMPRINT",EDGE,{"derivedFrom":makeQuery(id+"F1.opExtrude","CAP_EDGE",EDGE,{"disambiguationData":[OSD([subQ0])],"isStart":false})})])],"isStart":false});}
            var Q5;
            {var subQ0=sQuery(id+"F0.wireOp",EDGE,"E1.filletArc");Q5=makeQuery(id+"F23.opExtrude","CAP_EDGE",EDGE,{"disambiguationData":[OSD([subQ0]),TDD([makeQuery(id+"F4.imprint","IMPRINT",EDGE,{"derivedFrom":makeQuery(id+"F1.opExtrude","CAP_EDGE",EDGE,{"disambiguationData":[OSD([subQ0])],"isStart":false})})])],"isStart":false});}
            var Q6;
            {var subQ0=sQuery(id+"F0.wireOp",EDGE,"E0.left");Q6=makeQuery(id+"F23.opExtrude","CAP_EDGE",EDGE,{"disambiguationData":[OSD([subQ0]),TDD([makeQuery(id+"F4.imprint","IMPRINT",EDGE,{"derivedFrom":makeQuery(id+"F1.opExtrude","CAP_EDGE",EDGE,{"disambiguationData":[OSD([subQ0])],"isStart":false})})])],"isStart":false});}
            var Q7;
            {var subQ0=sQuery(id+"F0.wireOp",EDGE,"E4.filletArc");var subQ1=makeQuery(id+"F1.opExtrude","CAP_EDGE",EDGE,{"disambiguationData":[OSD([subQ0])],"isStart":false});Q7=makeQuery(id+"F23.opExtrude","CAP_EDGE",EDGE,{"disambiguationData":[OSD([subQ0]),TDD([makeQuery(id+"F4.imprint","IMPRINT",EDGE,{"disambiguationData":[TD([[makeQuery(id+"F4.imprint","INTERSECT",VERTEX,{"derivedFrom":[makeQuery(id+"F1.opExtrude","CAP_EDGE",EDGE,{"disambiguationData":[OSD([sQuery(id+"F0.wireOp",EDGE,"E0.left")])],"isStart":false}),subQ1]}),-1.0]])],"derivedFrom":subQ1})])],"isStart":false});}
            sweep(context, id + "F24", {"operationType" : NewBodyOperationType.ADD, "profiles" : qUnion([Q0]), "path" : qUnion([Q1, Q2, Q3, Q4, Q5, Q6, Q7])});
        }
        {
            var Q0;
            Q0=sQuery(id+"F15.wireOp",VERTEX,"E38");
            var Q1;
            Q1=makeQuery(id+"F22.boolean.opBoolean","SPLIT",BODY,{"disambiguationData":[OD(1.0)],"derivedFrom":makeQuery(id+"F1.opExtrude","SWEPT_BODY",BODY,{"disambiguationData":[OSD([sQuery(id+"F0.wireOp",EDGE,"E0.bottom"),sQuery(id+"F0.wireOp",EDGE,"E0.top"),sQuery(id+"F0.wireOp",EDGE,"E0.left"),sQuery(id+"F0.wireOp",EDGE,"E0.right"),sQuery(id+"F0.wireOp",EDGE,"E1.filletArc"),sQuery(id+"F0.wireOp",EDGE,"E2.filletArc"),sQuery(id+"F0.wireOp",EDGE,"E3.filletArc"),sQuery(id+"F0.wireOp",EDGE,"E4.filletArc"),sQuery(id+"F0.wireOp",EDGE,"E5.bottom"),sQuery(id+"F0.wireOp",EDGE,"E5.top"),sQuery(id+"F0.wireOp",EDGE,"E5.left"),sQuery(id+"F0.wireOp",EDGE,"E5.right"),sQuery(id+"F0.wireOp",EDGE,"E6.filletArc"),sQuery(id+"F0.wireOp",EDGE,"E7.filletArc"),sQuery(id+"F0.wireOp",EDGE,"E8.filletArc"),sQuery(id+"F0.wireOp",EDGE,"E9.filletArc")])]})});
            var Q2;
            Q2=makeQuery(id+"F22.boolean.opBoolean","SPLIT",BODY,{"disambiguationData":[OD(0.0)],"derivedFrom":makeQuery(id+"F1.opExtrude","SWEPT_BODY",BODY,{"disambiguationData":[OSD([sQuery(id+"F0.wireOp",EDGE,"E0.bottom"),sQuery(id+"F0.wireOp",EDGE,"E0.top"),sQuery(id+"F0.wireOp",EDGE,"E0.left"),sQuery(id+"F0.wireOp",EDGE,"E0.right"),sQuery(id+"F0.wireOp",EDGE,"E1.filletArc"),sQuery(id+"F0.wireOp",EDGE,"E2.filletArc"),sQuery(id+"F0.wireOp",EDGE,"E3.filletArc"),sQuery(id+"F0.wireOp",EDGE,"E4.filletArc"),sQuery(id+"F0.wireOp",EDGE,"E5.bottom"),sQuery(id+"F0.wireOp",EDGE,"E5.top"),sQuery(id+"F0.wireOp",EDGE,"E5.left"),sQuery(id+"F0.wireOp",EDGE,"E5.right"),sQuery(id+"F0.wireOp",EDGE,"E6.filletArc"),sQuery(id+"F0.wireOp",EDGE,"E7.filletArc"),sQuery(id+"F0.wireOp",EDGE,"E8.filletArc"),sQuery(id+"F0.wireOp",EDGE,"E9.filletArc")])]})});
            hole(context, id + "F25", {"style" : HoleStyle.C_SINK, "endStyle" : HoleEndStyle.BLIND, "holeDiameter" : 4 * mm, "cSinkDiameter" : 5 * mm, "cSinkAngle" : 90 * degree, "majorDiameter" : 5 * mm, "holeDepth" : 20 * mm, "isTappedThrough" : true, "tappedDepth" : 12 * mm, "tapClearance" : 3, "locations" : qUnion([Q0]), "scope" : qUnion([Q1, Q2])});
        }
        {
            var Q0;
            Q0=makeQuery(id+"F23.opExtrude","CAP_EDGE",EDGE,{"disambiguationData":[OSD([sQuery(id+"F0.wireOp",EDGE,"E12")])],"isStart":false});
            var Q1;
            Q1=makeQuery(id+"F23.opExtrude","CAP_EDGE",EDGE,{"disambiguationData":[OSD([sQuery(id+"F0.wireOp",EDGE,"E10")])],"isStart":false});
            var Q2;
            Q2=makeQuery(id+"F16.opExtrude","CAP_EDGE",EDGE,{"disambiguationData":[OSD([sQuery(id+"F15.wireOp",EDGE,"E36")])],"isStart":true});
            fillet(context, id + "F26", {"entities" : qUnion([Q0, Q1, Q2]), "radius" : 5 * mm, "tangentPropagation" : true, "allowEdgeOverflow" : false});
        }
        {
            var Q0;
            Q0=makeQuery(id+"F23.opExtrude","CAP_EDGE",EDGE,{"disambiguationData":[OSD([sQuery(id+"F0.wireOp",EDGE,"E0.bottom"),sQuery(id+"F0.wireOp",EDGE,"E0.top"),sQuery(id+"F0.wireOp",EDGE,"E0.left"),sQuery(id+"F0.wireOp",EDGE,"E0.right"),sQuery(id+"F0.wireOp",EDGE,"E1.filletArc"),sQuery(id+"F0.wireOp",EDGE,"E2.filletArc"),sQuery(id+"F0.wireOp",EDGE,"E3.filletArc"),sQuery(id+"F0.wireOp",EDGE,"E4.filletArc"),sQuery(id+"F0.wireOp",EDGE,"E5.bottom"),sQuery(id+"F0.wireOp",EDGE,"E5.top"),sQuery(id+"F0.wireOp",EDGE,"E5.left"),sQuery(id+"F0.wireOp",EDGE,"E5.right"),sQuery(id+"F0.wireOp",EDGE,"E6.filletArc"),sQuery(id+"F0.wireOp",EDGE,"E7.filletArc"),sQuery(id+"F0.wireOp",EDGE,"E8.filletArc"),sQuery(id+"F0.wireOp",EDGE,"E9.filletArc"),sQuery(id+"F0.wireOp",EDGE,"E10"),sQuery(id+"F0.wireOp",EDGE,"E11"),sQuery(id+"F0.wireOp",EDGE,"E12"),sQuery(id+"F21.wireOp",EDGE,"E46")])],"isStart":false});
            chamfer(context, id + "F27", {"entities" : qUnion([Q0]), "width" : 1.5 * mm});
        }
    });
